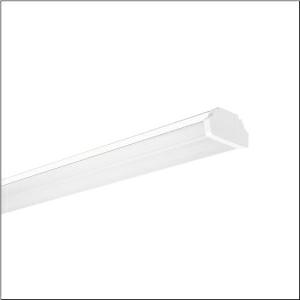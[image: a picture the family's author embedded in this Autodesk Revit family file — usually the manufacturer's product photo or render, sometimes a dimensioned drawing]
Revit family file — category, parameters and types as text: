
# Revit family: modario_31_gen_2_53bm812dv4f5d2_ed0a
name_source: partatom
category: Lighting Fixtures
units: mm (PartAtom-declared; Revit-internal decimal feet)

## family parameters
Cut with Voids When Loaded = No
Host = Face
Light Source = No
Part Type = Normal
Room Calculation Point = No
Round Connector Dimension = Use Diameter
Shared = No

## types (1)
- --- (1 x LED, 15730 lm, 87.2 W, 4000K)
    Apparent Load = 87 VA
    CIE Flux Codes = 47 80 95 93 100
    Color Rendering = 80
    Color Temperature = 4000K
    Default Elevation = 1800 mm
    Description = Modario 31 Gen.2, luminaire insert, of sheet steel, coil coated, white, length: 1.495mm, width: 81mm, height: 82mm, 5x system unit, system units: 299mm, LED rated luminous flux: 15.730lm, light colour: 840, SDCM (Standard Deviation of Colour Matching)MacAdam ≤ 3 SDCM (initial), control gear: DALI 2, control gear: ECG DALI, with plug, 5-pole, with phase selection, mains connection: 220..240V, AC, 50/60Hz, rated input power: 87W, through-wiring accessed according to module size, primary optical cover: cover, of PMMA, light emission: direct distribution, primary light characteristic: symmetric, protection rating (complete): IP20, protection rating (LED compartment): IP50, insulation class (complete): insulation class I (protective earthing), certification: CE, ENEC, VDE, UKCA, impact resistance: IK03, permissible ambient temperature for indoor applications: -25..+30°C, corresponds to IFS (International Featured Standards) requirements for safety and quality in the food industry, reducing of maximum allowable ambient temperature of 5°C with ceiling mounting, IP40 when using the optional accessory 5TP9018, packaging unit: 1 piece
    Height = 92 mm
    Lamp = 1 x LED
    Lamp Light Flux = 15730 lm
    Lamp Power = 87.2 W
    Lamp count = 1
    Length = 1495 mm
    Luminous efficacy = 180 lm/W
    Manufacturer = Siteco
    ModVariant = No
    Model = 53BM812DV4F5D2
    Mounting Place = Ceiling
    Mounting Type = Pendant
    Number of Poles = 1
    OnlyDefault = Yes
    Power Factor = 1
    Product Name = Modario 31 Gen.2
    Product group = luminaire insert | ceiling pendant
    ProductGroupID = 901
    Protection Class = Protection class I
    Protection Degree = IP 20
    RLX_Detail_Level = 1
    RLX_Emergency_Light_Flux = 0 lm
    RLX_Emergency_Type = 0
    RLX_Emergency_Type_DB = No
    RlxData = <blob elided: 42193 chars, md5=f6dad086>
    Socket = socket
    Standby Power = 0 W
    System Light Flux = 15730 lm
    System Power = 87 W
    Type Comments = factory setting: luminous flux: 100 % | dim-lin: 254 | 594 mA
    Type Image = l_1341886.jpg
    URL = http://relux.com
    VarID = @adj_052623
    Voltage = 0 V
    Weight = 0.00 kg
    Width = 81 mm

## geometry (parser evidence)
native form markers: Blend x4, Sweep x15
no freeform markers — native parametric forms only
